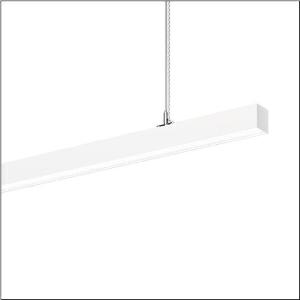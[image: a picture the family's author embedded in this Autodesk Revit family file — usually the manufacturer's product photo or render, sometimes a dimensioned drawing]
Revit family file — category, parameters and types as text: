
# Revit family: silica_r__21_51mx30da44wb_0345
name_source: partatom
category: Lighting Fixtures
units: mm (PartAtom-declared; Revit-internal decimal feet)

## family parameters
Cut with Voids When Loaded = No
Host = Face
Light Source = No
Part Type = Normal
Room Calculation Point = No
Round Connector Dimension = Use Diameter
Shared = No

## types (1)
- --- (1 x LED, 4210 lm, 26 W, 4000K)
    Apparent Load = 26 VA
    CIE Flux Codes = 47 79 96 57 100
    Color Rendering = 80
    Color Temperature = 4000K
    Default Elevation = 1800 mm
    Description = Silica® 21, office luminaire, primary optical cover: cover, of PMMA, opal, light emission: direct/indirect distribution, primary light characteristic: symmetric, installation type: suspended mounting, LED, rated luminous flux: 4.210lm, luminous efficacy: 162lm/W, light colour: 840, colour temperature: 4000K, with terminal, 3+2-pole, max. 2.5mm², mains connection: 220..240V, AC, 50/60Hz, rated input power: 26W, luminaire housing, of aluminium, traffic white (RAL 9016), length: 1.204mm, width: 53mm, height: 53mm, protection rating (complete): IP20, insulation class (complete): insulation class I (protective earthing), certification: CE, permissible operating ambient temperature: 0..+35°C, standard: EN 50419, packaging unit: 1 piece
    Height = 53 mm
    Lamp = 1 x LED
    Lamp Light Flux = 4210 lm
    Lamp Power = 26 W
    Lamp count = 1
    Length = 1204 mm
    Luminous efficacy = 162 lm/W
    Manufacturer = Siteco
    ModVariant = No
    Model = 51MX30DA44WB
    Mounting Place = Ceiling
    Mounting Type = Pendant
    Number of Poles = 1
    OnlyDefault = Yes
    Power Factor = 1
    Product Name = Silica® 21
    Product group = office luminaire | ceiling pendant
    ProductGroupID = 902
    Protection Class = Protection class I
    Protection Degree = IP 20
    RLX_Detail_Level = 1
    RLX_Emergency_Light_Flux = 0 lm
    RLX_Emergency_Type = 0
    RLX_Emergency_Type_DB = No
    RlxData = <blob elided: 21113 chars, md5=bd4cb348>
    Socket = socket
    Standby Power = 0 W
    System Light Flux = 4210 lm
    System Power = 26 W
    Type Comments = factory setting: luminous flux: 100 % | dim-lin: 254 | 218 mA
    Type Image = l_1297784.jpg
    URL = http://relux.com
    VarID = @adj_047553
    Voltage = 0 V
    Weight = 0.00 kg
    Width = 53 mm

## geometry (parser evidence)
native form markers: Blend x4, Sweep x11
no freeform markers — native parametric forms only
